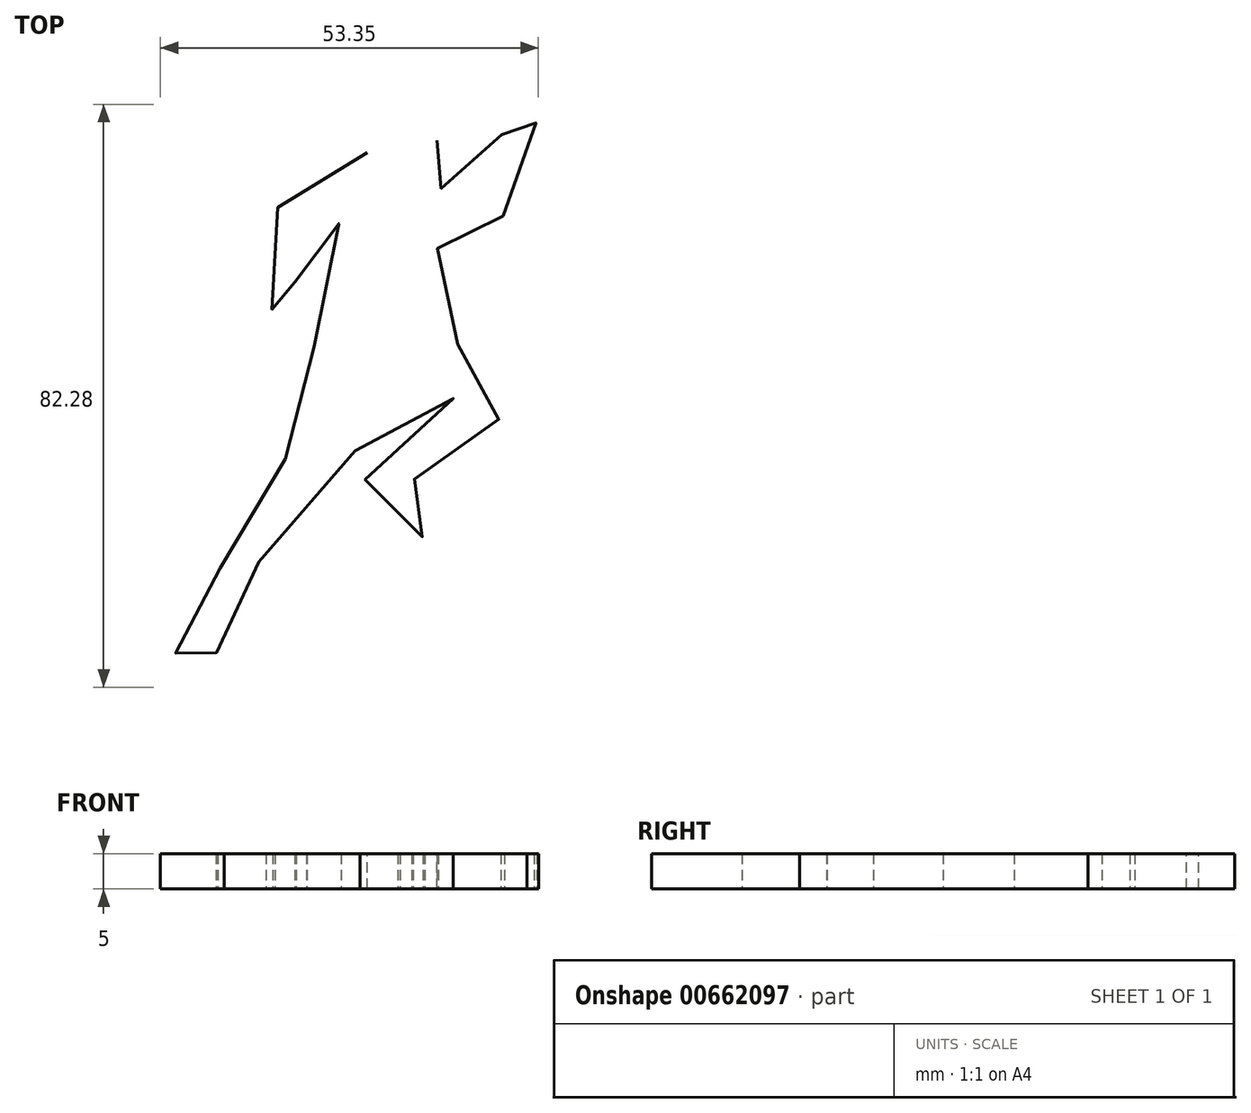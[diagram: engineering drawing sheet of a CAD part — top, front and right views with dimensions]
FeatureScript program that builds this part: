
annotation { "Feature Type Name" : "Feature", "Feature Type Description" : "" }
export const myFeature = defineFeature(function(context is Context, id is Id, definition is map)
    precondition{}
    {
        {
            var Q0;
            Q0=qCreatedBy(makeId("Top.planeOp"),FACE);
            var sketch = newSketch(context, id + "F0", { "sketchPlane" : qUnion([Q0])});
            skFitSpline(sketch, "E0", {"points": [v(-6.47, 11.97) * mm, v(-10.33, 9.07) * mm, v(-14.77, 8.1) * mm, v(-18.05, 6.18) * mm, v(-19.79, 0) * mm, v(-19.6, -5.21) * mm, v(-20.75, -8.69) * mm, v(-19.98, -10.04) * mm, v(-19.4, -11.39) * mm, v(-18.63, -11.97) * mm, v(-17.66, -12.35) * mm, v(-16.89, -11.39) * mm, v(-16.5, -8.3) * mm, v(-16.7, -5.6) * mm, v(-15.73, 0) * mm, v(-14, 3.09) * mm, v(-11.3, 3.67) * mm, v(-10.33, -5.98) * mm, v(-11.3, -11.2) * mm, v(-13.03, -13.9) * mm, v(-14.96, -18.34) * mm, v(-15.15, -23.94) * mm, v(-17.28, -28.57) * mm, v(-18.82, -33.78) * mm, v(-23.07, -38.6) * mm, v(-25.96, -43.43) * mm, v(-30.02, -50.38) * mm, v(-35.23, -51.15) * mm, v(-34.65, -55.98) * mm, v(-31.37, -62.15) * mm, v(-28.86, -63.5) * mm, v(-26.73, -62.73) * mm, v(-27.31, -60.22) * mm, v(-27.5, -56.36) * mm, v(-26.73, -55.01) * mm, v(-27.5, -54.24) * mm, v(-23.65, -48.26) * mm, v(-19.01, -42.66) * mm, v(-13.6, -37.83) * mm, v(-7.05, -29.15) * mm, v(-1.83, -25.67) * mm, v(-2.03, -24.13) * mm, v(5.5, -22.58) * mm, v(2.22, -26.64) * mm, v(-3.57, -32.24) * mm, v(-4.34, -32.24) * mm, v(-7.43, -35.52) * mm, v(-5.7, -37.45) * mm, v(-3.96, -38.8) * mm, v(-3.57, -38.8) * mm, v(0, -41.5) * mm, v(3.76, -42.47) * mm, v(5.7, -40.15) * mm, v(3.96, -39) * mm, v(0, -34.36) * mm, v(1.64, -33.59) * mm, v(1.45, -33.2) * mm, v(3.96, -31.27) * mm, v(10.33, -27.02) * mm, v(14.57, -23.55) * mm, v(16.12, -20.46) * mm, v(12.64, -16.4) * mm, v(0, -13.7) * mm, v(1.45, -10.8) * mm, v(3.57, -2.7) * mm, v(3.76, 0) * mm, v(9.94, -1.93) * mm, v(11.1, 0) * mm, v(12.45, 2.32) * mm, v(14.77, 9.84) * mm, v(17.47, 13.7) * mm, v(17.66, 14.48) * mm, v(17.08, 15.44) * mm, v(17.47, 16.8) * mm, v(16.12, 17.18) * mm, v(16.12, 17.95) * mm, v(15.54, 18.72) * mm, v(14.19, 18.34) * mm, v(12.45, 15.64) * mm, v(12.84, 10.8) * mm, v(8.78, 4.83) * mm, v(7.43, 5.02) * mm, v(3.18, 7.72) * mm, v(2.03, 9.84) * mm, v(0, 10.23) * mm, v(3, 11.97) * mm, v(3.38, 13.32) * mm, v(3.38, 13.7) * mm], "startDerivative": vector(-273.14, -259.41) * mm, "endDerivative": vector(4.85, 87.44) * mm});
            skSolve(sketch);
        }
        {
            var Q0;
            Q0=sQuery(id+"F0.wireOp",EDGE,"E0");
            extrude(context, id + "F1", {"bodyType" : ToolBodyType.SURFACE, "surfaceEntities" : qUnion([Q0]), "depth" : 5 * mm, "offsetDistance" : 25.4 * mm});
        }
    });
